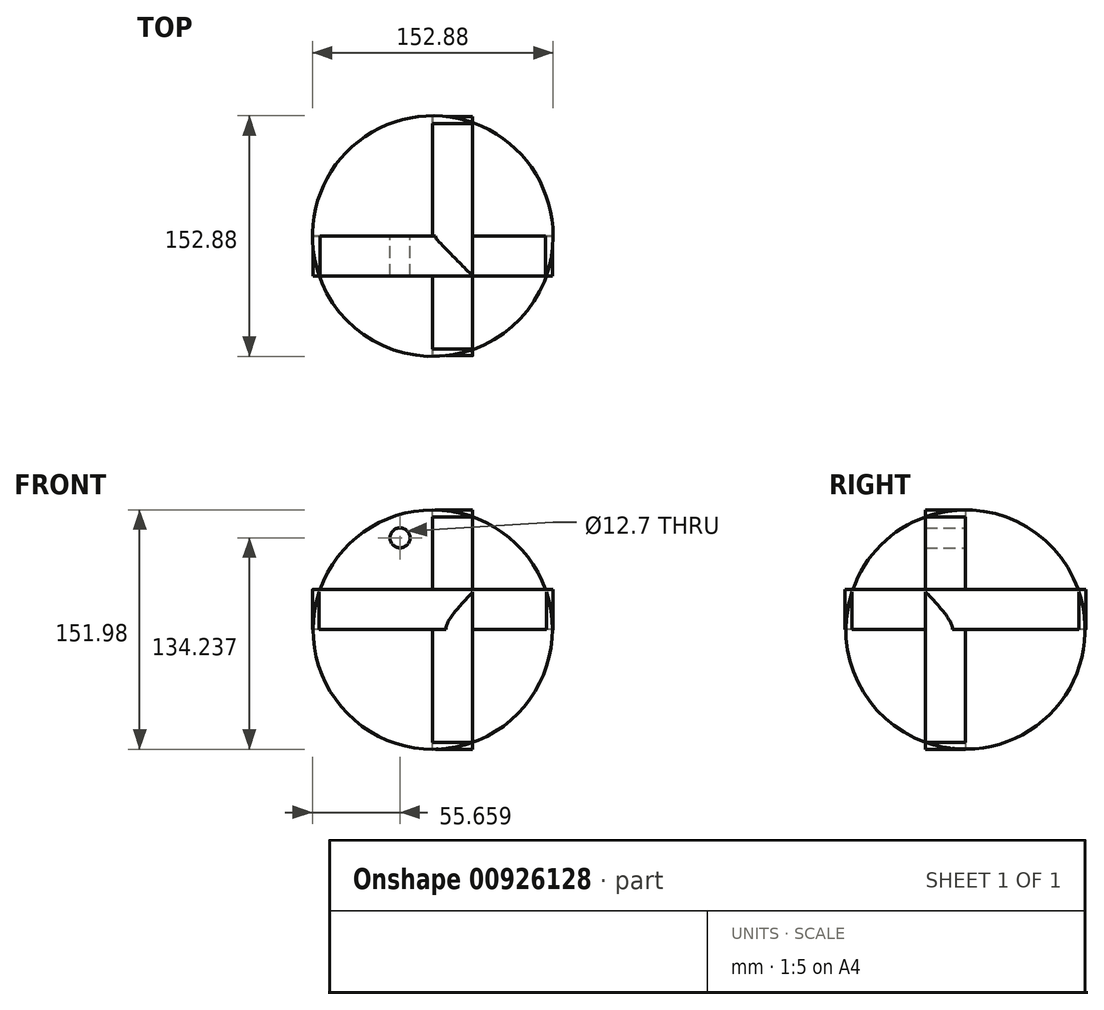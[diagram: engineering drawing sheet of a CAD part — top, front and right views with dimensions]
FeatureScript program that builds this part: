
annotation { "Feature Type Name" : "Feature", "Feature Type Description" : "" }
export const myFeature = defineFeature(function(context is Context, id is Id, definition is map)
    precondition{}
    {
        {
            var Q0;
            Q0=qCreatedBy(makeId("Front.planeOp"),FACE);
            var sketch = newSketch(context, id + "F0", { "sketchPlane" : qUnion([Q0])});
            skCircle(sketch, "E0", {"center": v(0, 0) * mm, "radius": 75.99 * mm});
            skSolve(sketch);
        }
        {
            var Q0;
            Q0=makeQuery(id+"F0.imprint","IMPRINT",FACE,{"disambiguationData":[TD([[makeQuery(id+"F0.imprint","IMPRINT",EDGE,{"derivedFrom":sQuery(id+"F0.wireOp",EDGE,"E0")}),1.0]])]});
            extrude(context, id + "F1", {"entities" : qUnion([Q0]), "depth" : 25.4 * mm, "offsetDistance" : 25.4 * mm});
        }
        {
            var Q0;
            Q0=qCreatedBy(makeId("Right.planeOp"),FACE);
            var sketch = newSketch(context, id + "F2", { "sketchPlane" : qUnion([Q0])});
            skCircle(sketch, "E1", {"center": v(0, 0) * mm, "radius": 75.97 * mm});
            skSolve(sketch);
        }
        {
            var Q0;
            Q0 = qSketchRegion(id + "F2", true);
            extrude(context, id + "F3", {"entities" : qUnion([Q0]), "operationType" : NewBodyOperationType.ADD, "depth" : 25.4 * mm, "offsetDistance" : 25.4 * mm});
        }
        {
            var Q0;
            Q0=qCreatedBy(makeId("Top.planeOp"),FACE);
            var sketch = newSketch(context, id + "F4", { "sketchPlane" : qUnion([Q0])});
            skCircle(sketch, "E2", {"center": v(0, 0) * mm, "radius": 76.44 * mm});
            skSolve(sketch);
        }
        {
            var Q0;
            Q0 = qSketchRegion(id + "F4", true);
            extrude(context, id + "F5", {"entities" : qUnion([Q0]), "operationType" : NewBodyOperationType.ADD, "depth" : 25.4 * mm, "offsetDistance" : 25.4 * mm});
        }
        {
            var Q0;
            Q0=qCreatedBy(makeId("Front.planeOp"),FACE);
            var sketch = newSketch(context, id + "F6", { "sketchPlane" : qUnion([Q0])});
            skCircle(sketch, "E3", {"center": v(-20.78, 58.25) * mm, "radius": 9.58 * mm});
            skSolve(sketch);
        }
        {
            var Q0;
            Q0=sQuery(id+"F6.wireOp",VERTEX,"E3.center");
            var Q1;
            Q1=makeQuery(id+"F1.opExtrude","SWEPT_BODY",BODY,{"disambiguationData":[OSD([sQuery(id+"F0.wireOp",EDGE,"E0")])]});
            hole(context, id + "F7", {"style" : HoleStyle.SIMPLE, "endStyle" : HoleEndStyle.THROUGH, "oppositeDirection" : true, "holeDiameter" : 12.7 * mm, "majorDiameter" : 6.35 * mm, "isTappedThrough" : true, "tappedDepth" : 12.7 * mm, "tapClearance" : 3, "locations" : qUnion([Q0]), "scope" : qUnion([Q1])});
        }
    });
